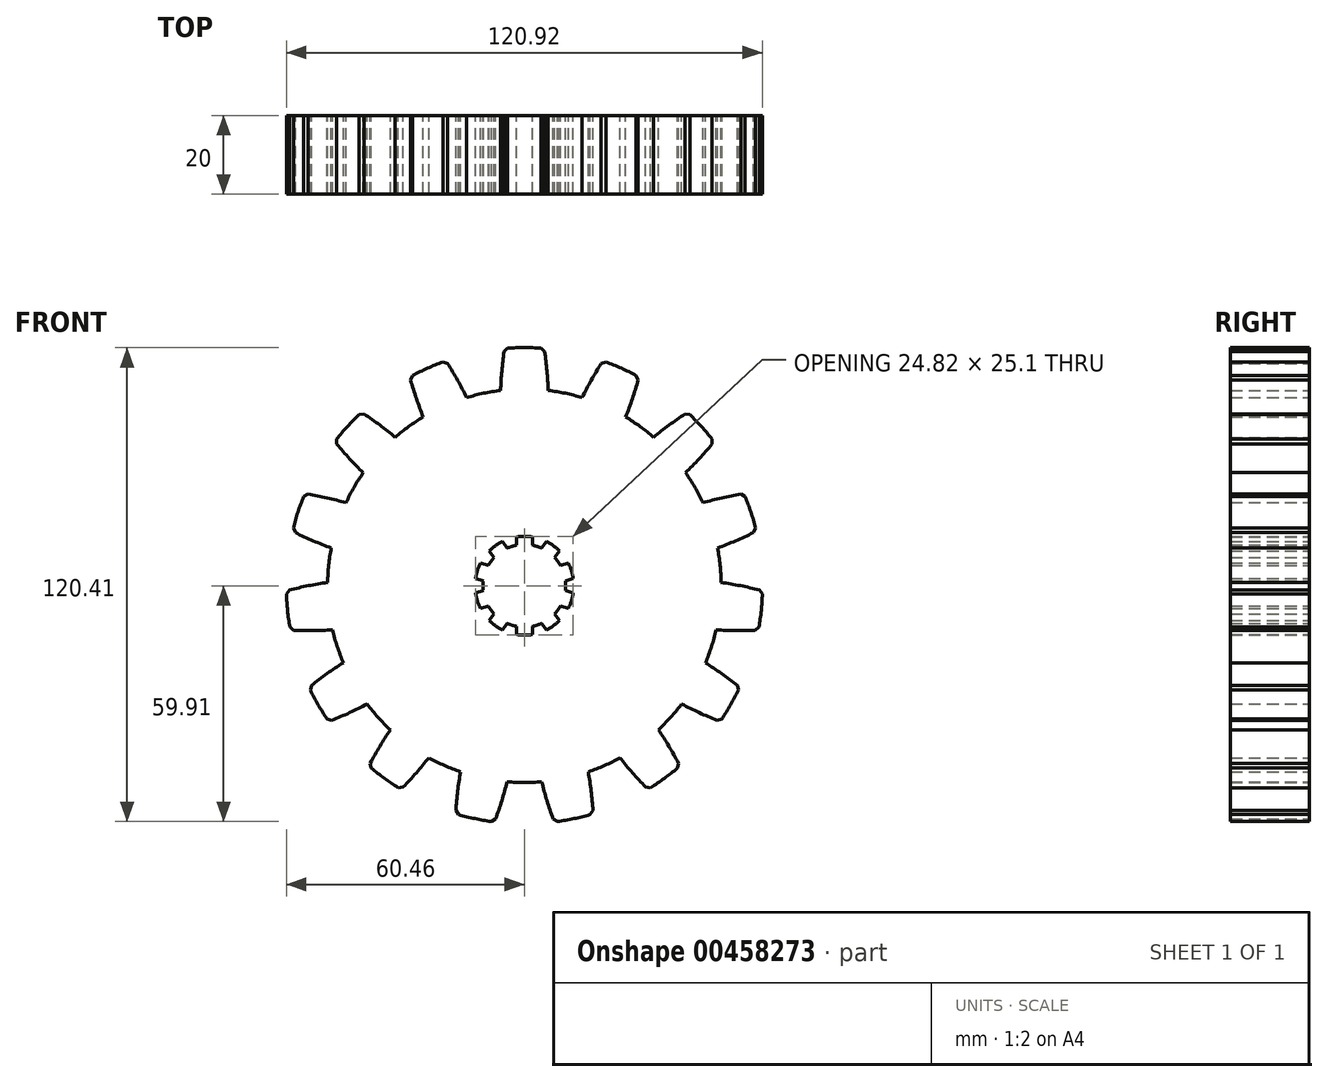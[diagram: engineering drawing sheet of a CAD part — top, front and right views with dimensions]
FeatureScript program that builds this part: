
annotation { "Feature Type Name" : "Feature", "Feature Type Description" : "" }
export const myFeature = defineFeature(function(context is Context, id is Id, definition is map)
    precondition{}
    {
        {
            var Q0;
            Q0=qCreatedBy(makeId("Front.planeOp"),FACE);
            var sketch = newSketch(context, id + "F0", { "sketchPlane" : qUnion([Q0])});
            skCircle(sketch, "E0", {"center": v(0, 0) * mm, "radius": 50 * mm});
            skLineSegment(sketch, "E1", {"start": v(0, 0) * mm, "end": v(0, 73.41) * mm, "construction": true});
            skLineSegment(sketch, "E2", {"start": v(0, 46.5) * mm, "end": v(83.9, 46.5) * mm, "construction": true});
            skLineSegment(sketch, "E3", {"start": v(83.9, 46.5) * mm, "end": v(23.98, 113.65) * mm});
            skArc(sketch, "E4", {"start": v(-5.04, 60.29) * mm, "mid": v(-5.7, 54.98) * mm, "end": v(-6.05, 49.63) * mm});
            skArc(sketch, "E5.MirrorC", {"start": v(5.04, 60.29) * mm, "mid": v(5.83, 53.42) * mm, "end": v(6.1, 46.5) * mm});
            skArc(sketch, "E6", {"start": v(5.04, 60.29) * mm, "mid": v(0, 60.5) * mm, "end": v(-5.04, 60.29) * mm});
            skArc(sketch, "E7.1.0", {"start": v(-29.12, 53.03) * mm, "mid": v(-27.57, 47.9) * mm, "end": v(-25.71, 42.88) * mm});
            skArc(sketch, "E7.1.1", {"start": v(-19.92, 57.13) * mm, "mid": v(-24.6, 55.27) * mm, "end": v(-29.12, 53.03) * mm});
            skArc(sketch, "E7.1.2", {"start": v(-19.92, 57.13) * mm, "mid": v(-16.4, 51.17) * mm, "end": v(-13.34, 44.96) * mm});
            skArc(sketch, "E7.2.0", {"start": v(-48.17, 36.6) * mm, "mid": v(-44.67, 32.55) * mm, "end": v(-40.93, 28.72) * mm});
            skArc(sketch, "E7.2.1", {"start": v(-41.43, 44.09) * mm, "mid": v(-44.96, 40.48) * mm, "end": v(-48.17, 36.6) * mm});
            skArc(sketch, "E7.2.2", {"start": v(-41.43, 44.09) * mm, "mid": v(-35.8, 40.08) * mm, "end": v(-30.47, 35.65) * mm});
            skArc(sketch, "E8.3.3.0", {"start": v(-58.9, 13.84) * mm, "mid": v(-54.05, 11.57) * mm, "end": v(-49.07, 9.59) * mm});
            skArc(sketch, "E8.4.3.0", {"start": v(-55.78, 23.42) * mm, "mid": v(-57.54, 18.7) * mm, "end": v(-58.9, 13.84) * mm});
            skArc(sketch, "E8.8.3.0", {"start": v(-55.78, 23.42) * mm, "mid": v(-49, 22.05) * mm, "end": v(-42.34, 20.17) * mm});
            skArc(sketch, "E8.3.4.0", {"start": v(-59.43, -11.31) * mm, "mid": v(-54.08, -11.42) * mm, "end": v(-48.73, -11.2) * mm});
            skArc(sketch, "E8.4.4.0", {"start": v(-60.49, -1.3) * mm, "mid": v(-60.17, -6.32) * mm, "end": v(-59.43, -11.31) * mm});
            skArc(sketch, "E8.8.4.0", {"start": v(-60.49, -1.3) * mm, "mid": v(-53.73, 0.22) * mm, "end": v(-46.88, 1.2) * mm});
            skArc(sketch, "E8.3.5.0", {"start": v(-49.7, -34.5) * mm, "mid": v(-44.76, -32.42) * mm, "end": v(-39.96, -30.05) * mm});
            skArc(sketch, "E8.4.5.0", {"start": v(-54.73, -25.78) * mm, "mid": v(-52.4, -30.25) * mm, "end": v(-49.7, -34.5) * mm});
            skArc(sketch, "E8.8.5.0", {"start": v(-54.73, -25.78) * mm, "mid": v(-49.18, -21.66) * mm, "end": v(-43.32, -17.97) * mm});
            skArc(sketch, "E8.3.6.0", {"start": v(-31.36, -51.74) * mm, "mid": v(-27.7, -47.83) * mm, "end": v(-24.28, -43.7) * mm});
            skArc(sketch, "E8.4.6.0", {"start": v(-39.51, -45.81) * mm, "mid": v(-35.56, -48.95) * mm, "end": v(-31.36, -51.74) * mm});
            skArc(sketch, "E8.8.6.0", {"start": v(-39.51, -45.81) * mm, "mid": v(-36.12, -39.78) * mm, "end": v(-32.27, -34.03) * mm});
            skArc(sketch, "E8.3.7.0", {"start": v(-7.6, -60.02) * mm, "mid": v(-5.85, -54.96) * mm, "end": v(-4.4, -49.8) * mm});
            skArc(sketch, "E8.4.7.0", {"start": v(-17.46, -57.93) * mm, "mid": v(-12.58, -59.18) * mm, "end": v(-7.6, -60.02) * mm});
            skArc(sketch, "E8.8.7.0", {"start": v(-17.46, -57.93) * mm, "mid": v(-16.81, -51.04) * mm, "end": v(-15.63, -44.22) * mm});
            skArc(sketch, "E8.3.8.0", {"start": v(17.46, -57.93) * mm, "mid": v(17, -52.6) * mm, "end": v(16.23, -47.3) * mm});
            skArc(sketch, "E8.4.8.0", {"start": v(7.6, -60.02) * mm, "mid": v(12.58, -59.18) * mm, "end": v(17.46, -57.93) * mm});
            skArc(sketch, "E8.8.8.0", {"start": v(7.6, -60.02) * mm, "mid": v(5.4, -53.46) * mm, "end": v(3.7, -46.75) * mm});
            skArc(sketch, "E8.3.9.0", {"start": v(39.51, -45.81) * mm, "mid": v(36.93, -41.13) * mm, "end": v(34.06, -36.6) * mm});
            skArc(sketch, "E8.4.9.0", {"start": v(31.36, -51.74) * mm, "mid": v(35.56, -48.95) * mm, "end": v(39.51, -45.81) * mm});
            skArc(sketch, "E8.8.9.0", {"start": v(31.36, -51.74) * mm, "mid": v(26.68, -46.64) * mm, "end": v(22.4, -41.2) * mm});
            skArc(sketch, "E8.3.10.0", {"start": v(54.73, -25.78) * mm, "mid": v(50.46, -22.55) * mm, "end": v(46, -19.58) * mm});
            skArc(sketch, "E8.4.10.0", {"start": v(49.7, -34.5) * mm, "mid": v(52.4, -30.25) * mm, "end": v(54.73, -25.78) * mm});
            skArc(sketch, "E8.8.10.0", {"start": v(49.7, -34.5) * mm, "mid": v(43.34, -31.76) * mm, "end": v(37.22, -28.53) * mm});
            skArc(sketch, "E8.3.11.0", {"start": v(60.49, -1.3) * mm, "mid": v(55.27, -0.08) * mm, "end": v(50, 0.82) * mm});
            skArc(sketch, "E8.4.11.0", {"start": v(59.43, -11.31) * mm, "mid": v(60.17, -6.32) * mm, "end": v(60.49, -1.3) * mm});
            skArc(sketch, "E8.8.11.0", {"start": v(59.43, -11.31) * mm, "mid": v(52.51, -11.39) * mm, "end": v(45.6, -10.93) * mm});
            skArc(sketch, "E8.3.12.0", {"start": v(55.78, 23.42) * mm, "mid": v(50.52, 22.4) * mm, "end": v(45.34, 21.09) * mm});
            skArc(sketch, "E8.4.12.0", {"start": v(58.9, 13.84) * mm, "mid": v(57.54, 18.7) * mm, "end": v(55.78, 23.42) * mm});
            skArc(sketch, "E8.8.12.0", {"start": v(58.9, 13.84) * mm, "mid": v(52.6, 10.96) * mm, "end": v(46.1, 8.57) * mm});
            skArc(sketch, "E8.3.13.0", {"start": v(41.43, 44.09) * mm, "mid": v(37.04, 41.02) * mm, "end": v(32.84, 37.7) * mm});
            skArc(sketch, "E8.4.13.0", {"start": v(48.17, 36.6) * mm, "mid": v(44.96, 40.48) * mm, "end": v(41.43, 44.09) * mm});
            skArc(sketch, "E8.8.13.0", {"start": v(48.17, 36.6) * mm, "mid": v(43.6, 31.4) * mm, "end": v(38.64, 26.58) * mm});
            skArc(sketch, "E8.3.14.0", {"start": v(19.92, 57.13) * mm, "mid": v(17.15, 52.54) * mm, "end": v(14.66, 47.8) * mm});
            skArc(sketch, "E8.4.14.0", {"start": v(29.12, 53.03) * mm, "mid": v(24.6, 55.27) * mm, "end": v(19.92, 57.13) * mm});
            skArc(sketch, "E8.8.14.0", {"start": v(29.12, 53.03) * mm, "mid": v(27.06, 46.42) * mm, "end": v(24.49, 40) * mm});
            skCircle(sketch, "E9", {"center": v(0, 0) * mm, "radius": 10.5 * mm});
            skArc(sketch, "E10", {"start": v(2.05, 12.38) * mm, "mid": v(0, 12.55) * mm, "end": v(-2.05, 12.38) * mm});
            skLineSegment(sketch, "E11.left", {"start": v(2.05, 10.3) * mm, "end": v(2.05, 12.38) * mm});
            skLineSegment(sketch, "E11.right", {"start": v(-2.05, 10.3) * mm, "end": v(-2.05, 12.38) * mm});
            skPoint(sketch, "E11.middle", {"position": v(0, 11.48) * mm});
            skPoint(sketch, "E12.orphan", {"position": v(2.05, 12.66) * mm});
            skPoint(sketch, "E13.orphan", {"position": v(-2.05, 12.66) * mm});
            skLineSegment(sketch, "E14.1.0", {"start": v(-4.4, 9.54) * mm, "end": v(-5.62, 11.22) * mm});
            skArc(sketch, "E14.1.1", {"start": v(-5.62, 11.22) * mm, "mid": v(-7.38, 10.15) * mm, "end": v(-8.94, 8.81) * mm});
            skLineSegment(sketch, "E14.1.2", {"start": v(-7.71, 7.13) * mm, "end": v(-8.94, 8.81) * mm});
            skLineSegment(sketch, "E14.2.0", {"start": v(-9.16, 5.13) * mm, "end": v(-11.14, 5.78) * mm});
            skArc(sketch, "E14.2.1", {"start": v(-11.14, 5.78) * mm, "mid": v(-11.94, 3.88) * mm, "end": v(-12.4, 1.88) * mm});
            skLineSegment(sketch, "E14.2.2", {"start": v(-10.43, 1.23) * mm, "end": v(-12.4, 1.88) * mm});
            skLineSegment(sketch, "E14.3.0", {"start": v(-10.43, -1.23) * mm, "end": v(-12.4, -1.88) * mm});
            skArc(sketch, "E14.3.1", {"start": v(-12.4, -1.88) * mm, "mid": v(-11.94, -3.88) * mm, "end": v(-11.14, -5.78) * mm});
            skLineSegment(sketch, "E14.3.2", {"start": v(-9.16, -5.13) * mm, "end": v(-11.14, -5.78) * mm});
            skLineSegment(sketch, "E14.4.0", {"start": v(-7.71, -7.13) * mm, "end": v(-8.94, -8.81) * mm});
            skArc(sketch, "E14.4.1", {"start": v(-8.94, -8.81) * mm, "mid": v(-7.38, -10.15) * mm, "end": v(-5.62, -11.22) * mm});
            skLineSegment(sketch, "E14.4.2", {"start": v(-4.4, -9.54) * mm, "end": v(-5.62, -11.22) * mm});
            skLineSegment(sketch, "E14.5.0", {"start": v(-2.05, -10.3) * mm, "end": v(-2.05, -12.38) * mm});
            skArc(sketch, "E14.5.1", {"start": v(-2.05, -12.38) * mm, "mid": v(0, -12.55) * mm, "end": v(2.05, -12.38) * mm});
            skLineSegment(sketch, "E14.5.2", {"start": v(2.05, -10.3) * mm, "end": v(2.05, -12.38) * mm});
            skLineSegment(sketch, "E14.6.0", {"start": v(4.4, -9.54) * mm, "end": v(5.62, -11.22) * mm});
            skArc(sketch, "E14.6.1", {"start": v(5.62, -11.22) * mm, "mid": v(7.38, -10.15) * mm, "end": v(8.94, -8.81) * mm});
            skLineSegment(sketch, "E14.6.2", {"start": v(7.71, -7.13) * mm, "end": v(8.94, -8.81) * mm});
            skLineSegment(sketch, "E14.7.0", {"start": v(9.16, -5.13) * mm, "end": v(11.14, -5.78) * mm});
            skArc(sketch, "E14.7.1", {"start": v(11.14, -5.78) * mm, "mid": v(11.94, -3.88) * mm, "end": v(12.4, -1.88) * mm});
            skLineSegment(sketch, "E14.7.2", {"start": v(10.43, -1.23) * mm, "end": v(12.4, -1.88) * mm});
            skLineSegment(sketch, "E14.8.0", {"start": v(10.43, 1.23) * mm, "end": v(12.4, 1.88) * mm});
            skArc(sketch, "E14.8.1", {"start": v(12.4, 1.88) * mm, "mid": v(11.94, 3.88) * mm, "end": v(11.14, 5.78) * mm});
            skLineSegment(sketch, "E14.8.2", {"start": v(9.16, 5.13) * mm, "end": v(11.14, 5.78) * mm});
            skLineSegment(sketch, "E14.9.0", {"start": v(7.71, 7.13) * mm, "end": v(8.94, 8.81) * mm});
            skArc(sketch, "E14.9.1", {"start": v(8.94, 8.81) * mm, "mid": v(7.38, 10.15) * mm, "end": v(5.62, 11.22) * mm});
            skLineSegment(sketch, "E14.9.2", {"start": v(4.4, 9.54) * mm, "end": v(5.62, 11.22) * mm});
            skSolve(sketch);
        }
        {
            var Q0;
            {var subQ0=sQuery(id+"F0.wireOp",EDGE,"E0");var subQ18=makeQuery(id+"F0.imprint","INTERSECT",VERTEX,{"derivedFrom":[subQ0,sQuery(id+"F0.wireOp",EDGE,"E8.3.11.0")]});Q0=makeQuery(id+"F0.imprint","IMPRINT",FACE,{"disambiguationData":[TD([[makeQuery(id+"F0.imprint","IMPRINT",EDGE,{"disambiguationData":[TD([[subQ18,-1.0]])],"derivedFrom":subQ0}),1.0]])]});}
            var Q1;
            {var subQ0=sQuery(id+"F0.wireOp",EDGE,"E7.2.0");Q1=makeQuery(id+"F0.imprint","IMPRINT",FACE,{"disambiguationData":[TD([[makeQuery(id+"F0.imprint","IMPRINT",EDGE,{"derivedFrom":subQ0}),1.0]])]});}
            var Q2;
            {var subQ0=sQuery(id+"F0.wireOp",EDGE,"E7.1.0");Q2=makeQuery(id+"F0.imprint","IMPRINT",FACE,{"disambiguationData":[TD([[makeQuery(id+"F0.imprint","IMPRINT",EDGE,{"derivedFrom":subQ0}),1.0]])]});}
            var Q3;
            {var subQ0=sQuery(id+"F0.wireOp",EDGE,"E4");Q3=makeQuery(id+"F0.imprint","IMPRINT",FACE,{"disambiguationData":[TD([[makeQuery(id+"F0.imprint","IMPRINT",EDGE,{"derivedFrom":subQ0}),1.0]])]});}
            var Q4;
            {var subQ0=sQuery(id+"F0.wireOp",EDGE,"E8.3.14.0");Q4=makeQuery(id+"F0.imprint","IMPRINT",FACE,{"disambiguationData":[TD([[makeQuery(id+"F0.imprint","IMPRINT",EDGE,{"derivedFrom":subQ0}),1.0]])]});}
            var Q5;
            {var subQ0=sQuery(id+"F0.wireOp",EDGE,"E8.3.13.0");Q5=makeQuery(id+"F0.imprint","IMPRINT",FACE,{"disambiguationData":[TD([[makeQuery(id+"F0.imprint","IMPRINT",EDGE,{"derivedFrom":subQ0}),1.0]])]});}
            var Q6;
            {var subQ0=sQuery(id+"F0.wireOp",EDGE,"E8.3.12.0");Q6=makeQuery(id+"F0.imprint","IMPRINT",FACE,{"disambiguationData":[TD([[makeQuery(id+"F0.imprint","IMPRINT",EDGE,{"derivedFrom":subQ0}),1.0]])]});}
            var Q7;
            {var subQ0=sQuery(id+"F0.wireOp",EDGE,"E8.3.11.0");Q7=makeQuery(id+"F0.imprint","IMPRINT",FACE,{"disambiguationData":[TD([[makeQuery(id+"F0.imprint","IMPRINT",EDGE,{"derivedFrom":subQ0}),1.0]])]});}
            var Q8;
            {var subQ0=sQuery(id+"F0.wireOp",EDGE,"E8.3.10.0");Q8=makeQuery(id+"F0.imprint","IMPRINT",FACE,{"disambiguationData":[TD([[makeQuery(id+"F0.imprint","IMPRINT",EDGE,{"derivedFrom":subQ0}),1.0]])]});}
            var Q9;
            {var subQ0=sQuery(id+"F0.wireOp",EDGE,"E8.3.9.0");Q9=makeQuery(id+"F0.imprint","IMPRINT",FACE,{"disambiguationData":[TD([[makeQuery(id+"F0.imprint","IMPRINT",EDGE,{"derivedFrom":subQ0}),1.0]])]});}
            var Q10;
            {var subQ0=sQuery(id+"F0.wireOp",EDGE,"E8.3.8.0");Q10=makeQuery(id+"F0.imprint","IMPRINT",FACE,{"disambiguationData":[TD([[makeQuery(id+"F0.imprint","IMPRINT",EDGE,{"derivedFrom":subQ0}),1.0]])]});}
            var Q11;
            {var subQ0=sQuery(id+"F0.wireOp",EDGE,"E8.3.7.0");Q11=makeQuery(id+"F0.imprint","IMPRINT",FACE,{"disambiguationData":[TD([[makeQuery(id+"F0.imprint","IMPRINT",EDGE,{"derivedFrom":subQ0}),1.0]])]});}
            var Q12;
            {var subQ0=sQuery(id+"F0.wireOp",EDGE,"E8.3.6.0");Q12=makeQuery(id+"F0.imprint","IMPRINT",FACE,{"disambiguationData":[TD([[makeQuery(id+"F0.imprint","IMPRINT",EDGE,{"derivedFrom":subQ0}),1.0]])]});}
            var Q13;
            {var subQ0=sQuery(id+"F0.wireOp",EDGE,"E8.3.5.0");Q13=makeQuery(id+"F0.imprint","IMPRINT",FACE,{"disambiguationData":[TD([[makeQuery(id+"F0.imprint","IMPRINT",EDGE,{"derivedFrom":subQ0}),1.0]])]});}
            var Q14;
            {var subQ0=sQuery(id+"F0.wireOp",EDGE,"E8.3.4.0");Q14=makeQuery(id+"F0.imprint","IMPRINT",FACE,{"disambiguationData":[TD([[makeQuery(id+"F0.imprint","IMPRINT",EDGE,{"derivedFrom":subQ0}),1.0]])]});}
            var Q15;
            {var subQ0=sQuery(id+"F0.wireOp",EDGE,"E8.3.3.0");Q15=makeQuery(id+"F0.imprint","IMPRINT",FACE,{"disambiguationData":[TD([[makeQuery(id+"F0.imprint","IMPRINT",EDGE,{"derivedFrom":subQ0}),1.0]])]});}
            extrude(context, id + "F1", {"entities" : qUnion([Q0, Q1, Q2, Q3, Q4, Q5, Q6, Q7, Q8, Q9, Q10, Q11, Q12, Q13, Q14, Q15]), "depth" : 20 * mm});
        }
        {
            var Q0;
            Q0=makeQuery(id+"F1.opExtrude","SWEPT_EDGE",EDGE,{"disambiguationData":[OSD([sQuery(id+"F0.wireOp",EDGE,"E5.MirrorC"),sQuery(id+"F0.wireOp",EDGE,"E6")])]});
            var Q1;
            Q1=makeQuery(id+"F1.opExtrude","SWEPT_EDGE",EDGE,{"disambiguationData":[OSD([sQuery(id+"F0.wireOp",EDGE,"E4"),sQuery(id+"F0.wireOp",EDGE,"E6")])]});
            var Q2;
            Q2=makeQuery(id+"F1.opExtrude","SWEPT_EDGE",EDGE,{"disambiguationData":[OSD([sQuery(id+"F0.wireOp",EDGE,"E7.1.1"),sQuery(id+"F0.wireOp",EDGE,"E7.1.2")])]});
            var Q3;
            Q3=makeQuery(id+"F1.opExtrude","SWEPT_EDGE",EDGE,{"disambiguationData":[OSD([sQuery(id+"F0.wireOp",EDGE,"E7.1.0"),sQuery(id+"F0.wireOp",EDGE,"E7.1.1")])]});
            var Q4;
            Q4=makeQuery(id+"F1.opExtrude","SWEPT_EDGE",EDGE,{"disambiguationData":[OSD([sQuery(id+"F0.wireOp",EDGE,"E7.2.1"),sQuery(id+"F0.wireOp",EDGE,"E7.2.2")])]});
            var Q5;
            Q5=makeQuery(id+"F1.opExtrude","SWEPT_EDGE",EDGE,{"disambiguationData":[OSD([sQuery(id+"F0.wireOp",EDGE,"E7.2.0"),sQuery(id+"F0.wireOp",EDGE,"E7.2.1")])]});
            var Q6;
            Q6=makeQuery(id+"F1.opExtrude","SWEPT_EDGE",EDGE,{"disambiguationData":[OSD([sQuery(id+"F0.wireOp",EDGE,"E8.4.3.0"),sQuery(id+"F0.wireOp",EDGE,"E8.8.3.0")])]});
            var Q7;
            Q7=makeQuery(id+"F1.opExtrude","SWEPT_EDGE",EDGE,{"disambiguationData":[OSD([sQuery(id+"F0.wireOp",EDGE,"E8.3.3.0"),sQuery(id+"F0.wireOp",EDGE,"E8.4.3.0")])]});
            var Q8;
            Q8=makeQuery(id+"F1.opExtrude","SWEPT_EDGE",EDGE,{"disambiguationData":[OSD([sQuery(id+"F0.wireOp",EDGE,"E8.4.4.0"),sQuery(id+"F0.wireOp",EDGE,"E8.8.4.0")])]});
            var Q9;
            Q9=makeQuery(id+"F1.opExtrude","SWEPT_EDGE",EDGE,{"disambiguationData":[OSD([sQuery(id+"F0.wireOp",EDGE,"E8.3.4.0"),sQuery(id+"F0.wireOp",EDGE,"E8.4.4.0")])]});
            var Q10;
            Q10=makeQuery(id+"F1.opExtrude","SWEPT_EDGE",EDGE,{"disambiguationData":[OSD([sQuery(id+"F0.wireOp",EDGE,"E8.4.5.0"),sQuery(id+"F0.wireOp",EDGE,"E8.8.5.0")])]});
            var Q11;
            Q11=makeQuery(id+"F1.opExtrude","SWEPT_EDGE",EDGE,{"disambiguationData":[OSD([sQuery(id+"F0.wireOp",EDGE,"E8.3.5.0"),sQuery(id+"F0.wireOp",EDGE,"E8.4.5.0")])]});
            var Q12;
            Q12=makeQuery(id+"F1.opExtrude","SWEPT_EDGE",EDGE,{"disambiguationData":[OSD([sQuery(id+"F0.wireOp",EDGE,"E8.3.6.0"),sQuery(id+"F0.wireOp",EDGE,"E8.4.6.0")])]});
            var Q13;
            Q13=makeQuery(id+"F1.opExtrude","SWEPT_EDGE",EDGE,{"disambiguationData":[OSD([sQuery(id+"F0.wireOp",EDGE,"E8.4.6.0"),sQuery(id+"F0.wireOp",EDGE,"E8.8.6.0")])]});
            var Q14;
            Q14=makeQuery(id+"F1.opExtrude","SWEPT_EDGE",EDGE,{"disambiguationData":[OSD([sQuery(id+"F0.wireOp",EDGE,"E8.4.7.0"),sQuery(id+"F0.wireOp",EDGE,"E8.8.7.0")])]});
            var Q15;
            Q15=makeQuery(id+"F1.opExtrude","SWEPT_EDGE",EDGE,{"disambiguationData":[OSD([sQuery(id+"F0.wireOp",EDGE,"E8.3.7.0"),sQuery(id+"F0.wireOp",EDGE,"E8.4.7.0")])]});
            var Q16;
            Q16=makeQuery(id+"F1.opExtrude","SWEPT_EDGE",EDGE,{"disambiguationData":[OSD([sQuery(id+"F0.wireOp",EDGE,"E8.4.8.0"),sQuery(id+"F0.wireOp",EDGE,"E8.8.8.0")])]});
            var Q17;
            Q17=makeQuery(id+"F1.opExtrude","SWEPT_EDGE",EDGE,{"disambiguationData":[OSD([sQuery(id+"F0.wireOp",EDGE,"E8.3.8.0"),sQuery(id+"F0.wireOp",EDGE,"E8.4.8.0")])]});
            var Q18;
            Q18=makeQuery(id+"F1.opExtrude","SWEPT_EDGE",EDGE,{"disambiguationData":[OSD([sQuery(id+"F0.wireOp",EDGE,"E8.4.9.0"),sQuery(id+"F0.wireOp",EDGE,"E8.8.9.0")])]});
            var Q19;
            Q19=makeQuery(id+"F1.opExtrude","SWEPT_EDGE",EDGE,{"disambiguationData":[OSD([sQuery(id+"F0.wireOp",EDGE,"E8.3.9.0"),sQuery(id+"F0.wireOp",EDGE,"E8.4.9.0")])]});
            var Q20;
            Q20=makeQuery(id+"F1.opExtrude","SWEPT_EDGE",EDGE,{"disambiguationData":[OSD([sQuery(id+"F0.wireOp",EDGE,"E8.3.10.0"),sQuery(id+"F0.wireOp",EDGE,"E8.4.10.0")])]});
            var Q21;
            Q21=makeQuery(id+"F1.opExtrude","SWEPT_EDGE",EDGE,{"disambiguationData":[OSD([sQuery(id+"F0.wireOp",EDGE,"E8.4.10.0"),sQuery(id+"F0.wireOp",EDGE,"E8.8.10.0")])]});
            var Q22;
            Q22=makeQuery(id+"F1.opExtrude","SWEPT_EDGE",EDGE,{"disambiguationData":[OSD([sQuery(id+"F0.wireOp",EDGE,"E8.4.11.0"),sQuery(id+"F0.wireOp",EDGE,"E8.8.11.0")])]});
            var Q23;
            Q23=makeQuery(id+"F1.opExtrude","SWEPT_EDGE",EDGE,{"disambiguationData":[OSD([sQuery(id+"F0.wireOp",EDGE,"E8.3.11.0"),sQuery(id+"F0.wireOp",EDGE,"E8.4.11.0")])]});
            var Q24;
            Q24=makeQuery(id+"F1.opExtrude","SWEPT_EDGE",EDGE,{"disambiguationData":[OSD([sQuery(id+"F0.wireOp",EDGE,"E8.3.12.0"),sQuery(id+"F0.wireOp",EDGE,"E8.4.12.0")])]});
            var Q25;
            Q25=makeQuery(id+"F1.opExtrude","SWEPT_EDGE",EDGE,{"disambiguationData":[OSD([sQuery(id+"F0.wireOp",EDGE,"E8.4.12.0"),sQuery(id+"F0.wireOp",EDGE,"E8.8.12.0")])]});
            var Q26;
            Q26=makeQuery(id+"F1.opExtrude","SWEPT_EDGE",EDGE,{"disambiguationData":[OSD([sQuery(id+"F0.wireOp",EDGE,"E8.4.13.0"),sQuery(id+"F0.wireOp",EDGE,"E8.8.13.0")])]});
            var Q27;
            Q27=makeQuery(id+"F1.opExtrude","SWEPT_EDGE",EDGE,{"disambiguationData":[OSD([sQuery(id+"F0.wireOp",EDGE,"E8.3.13.0"),sQuery(id+"F0.wireOp",EDGE,"E8.4.13.0")])]});
            var Q28;
            Q28=makeQuery(id+"F1.opExtrude","SWEPT_EDGE",EDGE,{"disambiguationData":[OSD([sQuery(id+"F0.wireOp",EDGE,"E8.4.14.0"),sQuery(id+"F0.wireOp",EDGE,"E8.8.14.0")])]});
            var Q29;
            Q29=makeQuery(id+"F1.opExtrude","SWEPT_EDGE",EDGE,{"disambiguationData":[OSD([sQuery(id+"F0.wireOp",EDGE,"E8.3.14.0"),sQuery(id+"F0.wireOp",EDGE,"E8.4.14.0")])]});
            chamfer(context, id + "F2", {"entities" : qUnion([Q0, Q1, Q2, Q3, Q4, Q5, Q6, Q7, Q8, Q9, Q10, Q11, Q12, Q13, Q14, Q15, Q16, Q17, Q18, Q19, Q20, Q21, Q22, Q23, Q24, Q25, Q26, Q27, Q28, Q29]), "width" : 1 * mm, "tangentPropagation" : true});
        }
    });
